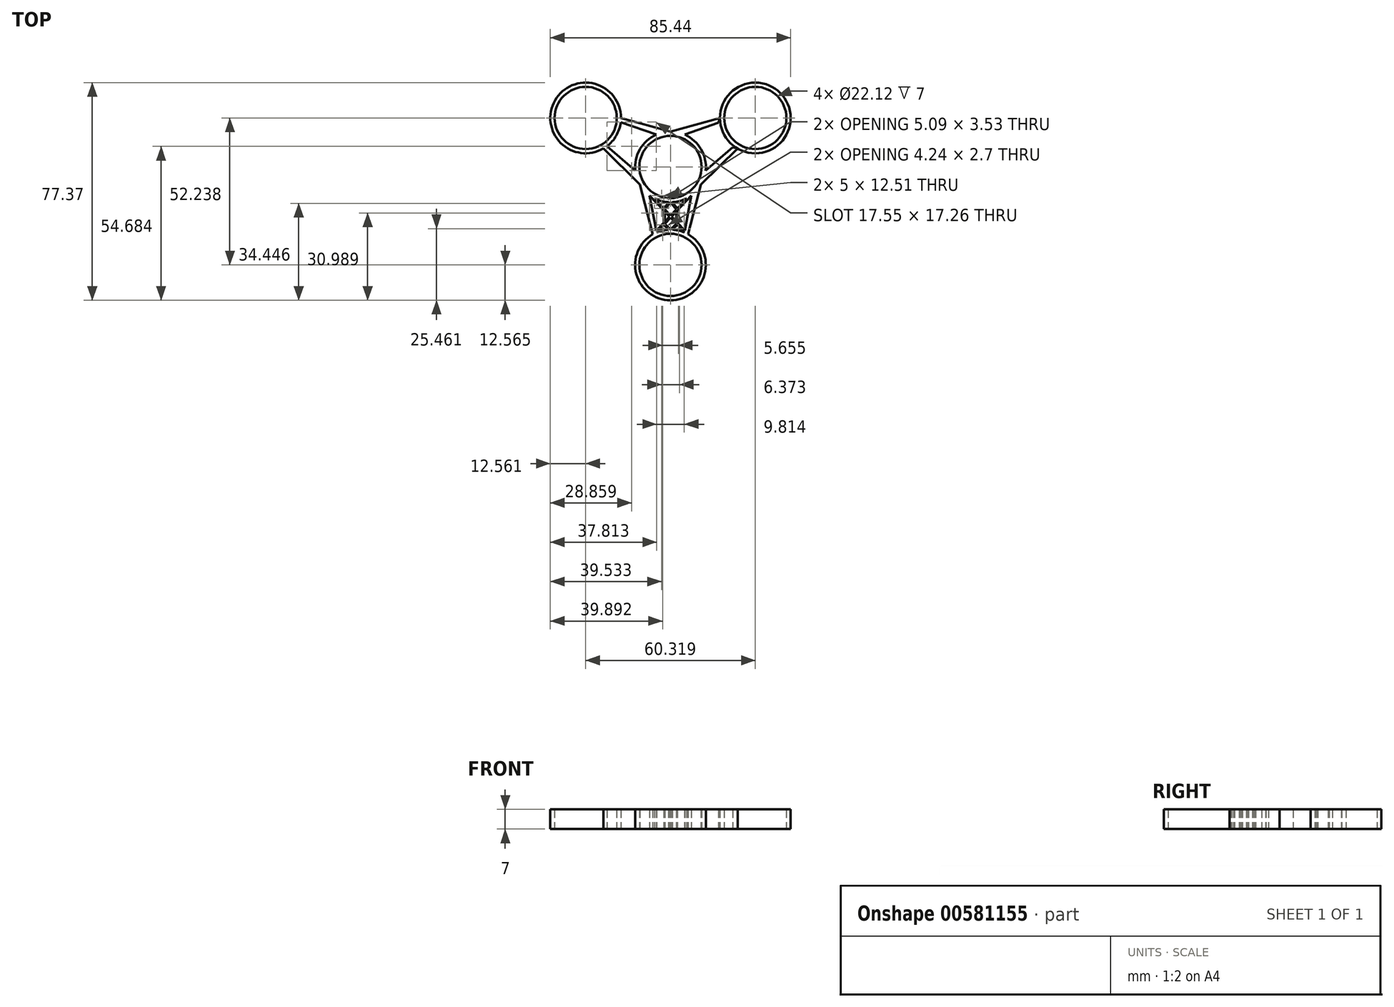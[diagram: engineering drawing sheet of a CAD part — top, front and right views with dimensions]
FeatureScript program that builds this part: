
annotation { "Feature Type Name" : "Feature", "Feature Type Description" : "" }
export const myFeature = defineFeature(function(context is Context, id is Id, definition is map)
    precondition{}
    {
        {
            var Q0;
            Q0=qCreatedBy(makeId("Top.planeOp"),FACE);
            var sketch = newSketch(context, id + "F0", { "sketchPlane" : qUnion([Q0])});
            skCircle(sketch, "E0", {"center": v(0, 0) * mm, "radius": 11.06 * mm});
            skCircle(sketch, "E1", {"center": v(-30.16, 17.41) * mm, "radius": 11.06 * mm});
            skCircle(sketch, "E2", {"center": v(-30.16, 17.41) * mm, "radius": 12.56 * mm});
            skCircle(sketch, "E3", {"center": v(0, -34.82) * mm, "radius": 11.06 * mm});
            skCircle(sketch, "E4", {"center": v(0, -34.82) * mm, "radius": 12.56 * mm});
            skCircle(sketch, "E5", {"center": v(30.16, 17.41) * mm, "radius": 11.06 * mm});
            skCircle(sketch, "E6", {"center": v(30.16, 17.41) * mm, "radius": 12.56 * mm});
            skCircle(sketch, "E7", {"center": v(0, 0) * mm, "radius": 12.56 * mm});
            skLineSegment(sketch, "E8", {"start": v(-30.16, 17.41) * mm, "end": v(0, -34.83) * mm, "construction": true});
            skLineSegment(sketch, "E9", {"start": v(0, -34.82) * mm, "end": v(30.16, 17.41) * mm, "construction": true});
            skLineSegment(sketch, "E10", {"start": v(30.16, 17.41) * mm, "end": v(-30.16, 17.41) * mm, "construction": true});
            skLineSegment(sketch, "E11", {"start": v(0, 0) * mm, "end": v(0, -34.82) * mm, "construction": true});
            skLineSegment(sketch, "E12", {"start": v(-23.88, 6.53) * mm, "end": v(-10.88, -6.28) * mm});
            skLineSegment(sketch, "E13", {"start": v(-10.88, -6.28) * mm, "end": v(-6.28, -23.95) * mm});
            skLineSegment(sketch, "E14", {"start": v(-17.6, 17.41) * mm, "end": v(0, 12.56) * mm});
            skLineSegment(sketch, "E15", {"start": v(0, 12.56) * mm, "end": v(17.6, 17.41) * mm});
            skLineSegment(sketch, "E16", {"start": v(23.88, 6.53) * mm, "end": v(10.88, -6.28) * mm});
            skLineSegment(sketch, "E17", {"start": v(10.88, -6.28) * mm, "end": v(6.28, -23.95) * mm});
            skLineSegment(sketch, "E18", {"start": v(-7.4, -10.15) * mm, "end": v(-4.95, -23.28) * mm});
            skLineSegment(sketch, "E19", {"start": v(7.4, -10.15) * mm, "end": v(4.95, -23.28) * mm});
            skLineSegment(sketch, "E20", {"start": v(12.5, -1.34) * mm, "end": v(22.63, 7.35) * mm});
            skLineSegment(sketch, "E21", {"start": v(17.69, 15.93) * mm, "end": v(5.09, 11.49) * mm});
            skLineSegment(sketch, "E22", {"start": v(-22.63, 7.35) * mm, "end": v(-12.5, -1.34) * mm});
            skLineSegment(sketch, "E23", {"start": v(-5.09, 11.49) * mm, "end": v(-17.69, 15.93) * mm});
            skLineSegment(sketch, "E24", {"start": v(-30.16, 17.41) * mm, "end": v(30.16, 17.41) * mm});
            skLineSegment(sketch, "E25", {"start": v(-4.95, -23.28) * mm, "end": v(7.4, -10.15) * mm});
            skLineSegment(sketch, "E26", {"start": v(4.95, -23.28) * mm, "end": v(-7.4, -10.15) * mm});
            skLineSegment(sketch, "E27", {"start": v(-6.28, -23.95) * mm, "end": v(5.73, -11.18) * mm});
            skLineSegment(sketch, "E28", {"start": v(6.28, -23.95) * mm, "end": v(-5.73, -11.18) * mm});
            skPoint(sketch, "E29", {"position": v(0, -22.26) * mm});
            skPoint(sketch, "E30", {"position": v(0, -18.02) * mm});
            skPoint(sketch, "E31", {"position": v(-0.35, -17.64) * mm});
            skPoint(sketch, "E32", {"position": v(0.35, -17.64) * mm});
            skPoint(sketch, "E33", {"position": v(0, -17.27) * mm});
            skPoint(sketch, "E34", {"position": v(0, -12.56) * mm});
            skLineSegment(sketch, "E35", {"start": v(-2.06, -20.2) * mm, "end": v(0, -22.26) * mm});
            skLineSegment(sketch, "E36", {"start": v(0, -22.26) * mm, "end": v(2.06, -20.2) * mm});
            skLineSegment(sketch, "E37", {"start": v(-2.4, -20.58) * mm, "end": v(-0.7, -22.28) * mm});
            skLineSegment(sketch, "E38", {"start": v(2.4, -20.58) * mm, "end": v(0.7, -22.28) * mm});
            skLineSegment(sketch, "E39", {"start": v(-2.06, -20.2) * mm, "end": v(-2.06, -15.08) * mm});
            skLineSegment(sketch, "E40", {"start": v(-2.4, -20.58) * mm, "end": v(-2.4, -14.7) * mm});
            skLineSegment(sketch, "E41", {"start": v(2.06, -20.2) * mm, "end": v(2.06, -15.08) * mm});
            skLineSegment(sketch, "E42", {"start": v(2.4, -20.58) * mm, "end": v(2.4, -14.7) * mm});
            skLineSegment(sketch, "E43", {"start": v(-2.06, -15.08) * mm, "end": v(0, -12.56) * mm});
            skLineSegment(sketch, "E44", {"start": v(2.06, -15.08) * mm, "end": v(0, -12.56) * mm});
            skLineSegment(sketch, "E45", {"start": v(-2.4, -14.7) * mm, "end": v(-0.64, -12.55) * mm});
            skLineSegment(sketch, "E46", {"start": v(2.4, -14.7) * mm, "end": v(0.64, -12.55) * mm});
            skLineSegment(sketch, "E47", {"start": v(17.69, 15.93) * mm, "end": v(12.5, -1.34) * mm});
            skLineSegment(sketch, "E48", {"start": v(17.6, 17.41) * mm, "end": v(12.55, 0.63) * mm});
            skLineSegment(sketch, "E49", {"start": v(22.63, 7.35) * mm, "end": v(5.09, 11.49) * mm});
            skLineSegment(sketch, "E50", {"start": v(23.88, 6.53) * mm, "end": v(6.82, 10.55) * mm});
            skLineSegment(sketch, "E51", {"start": v(0, 0) * mm, "end": v(30.16, 17.41) * mm, "construction": true});
            skLineSegment(sketch, "E52", {"start": v(0, 0) * mm, "end": v(-30.16, 17.41) * mm, "construction": true});
            skPoint(sketch, "E53", {"position": v(10.88, 6.28) * mm});
            skPoint(sketch, "E54", {"position": v(19.28, 11.13) * mm});
            skPoint(sketch, "E55", {"position": v(15.46, 8.52) * mm});
            skPoint(sketch, "E56", {"position": v(15.1, 9.13) * mm});
            skPoint(sketch, "E57", {"position": v(14.96, 8.63) * mm});
            skPoint(sketch, "E58", {"position": v(15.6, 9) * mm});
            skLineSegment(sketch, "E59", {"start": v(19.28, 11.13) * mm, "end": v(18.53, 8.32) * mm});
            skLineSegment(sketch, "E60", {"start": v(19.28, 11.13) * mm, "end": v(16.47, 11.88) * mm});
            skLineSegment(sketch, "E61", {"start": v(19.65, 10.53) * mm, "end": v(19.03, 8.2) * mm});
            skLineSegment(sketch, "E62", {"start": v(18.94, 11.75) * mm, "end": v(16.62, 12.38) * mm});
            skLineSegment(sketch, "E63", {"start": v(18.53, 8.32) * mm, "end": v(14.22, 6.18) * mm});
            skLineSegment(sketch, "E64", {"start": v(19.03, 8.2) * mm, "end": v(14.06, 5.66) * mm});
            skSolve(sketch);
        }
        {
            var Q0;
            {var subQ0=sQuery(id+"F0.wireOp",EDGE,"E12");Q0=makeQuery(id+"F0.imprint","IMPRINT",FACE,{"disambiguationData":[TD([[makeQuery(id+"F0.imprint","IMPRINT",EDGE,{"derivedFrom":subQ0}),1.0]])]});}
            var Q1;
            Q1=makeQuery(id+"F0.imprint","IMPRINT",FACE,{"disambiguationData":[TD([[makeQuery(id+"F0.imprint","IMPRINT",EDGE,{"derivedFrom":sQuery(id+"F0.wireOp",EDGE,"E1")}),-1.0]])]});
            var Q2;
            {var subQ0=sQuery(id+"F0.wireOp",EDGE,"E14");Q2=makeQuery(id+"F0.imprint","IMPRINT",FACE,{"disambiguationData":[TD([[makeQuery(id+"F0.imprint","IMPRINT",EDGE,{"derivedFrom":subQ0}),-1.0]])]});}
            var Q3;
            Q3=makeQuery(id+"F0.imprint","IMPRINT",FACE,{"disambiguationData":[TD([[makeQuery(id+"F0.imprint","IMPRINT",EDGE,{"derivedFrom":sQuery(id+"F0.wireOp",EDGE,"E0")}),-1.0]])]});
            var Q4;
            {var subQ0=sQuery(id+"F0.wireOp",EDGE,"E15");Q4=makeQuery(id+"F0.imprint","IMPRINT",FACE,{"disambiguationData":[TD([[makeQuery(id+"F0.imprint","IMPRINT",EDGE,{"derivedFrom":subQ0}),-1.0]])]});}
            var Q5;
            {var subQ0=sQuery(id+"F0.wireOp",EDGE,"E16");Q5=makeQuery(id+"F0.imprint","IMPRINT",FACE,{"disambiguationData":[TD([[makeQuery(id+"F0.imprint","IMPRINT",EDGE,{"derivedFrom":subQ0}),-1.0]])]});}
            var Q6;
            Q6=makeQuery(id+"F0.imprint","IMPRINT",FACE,{"disambiguationData":[TD([[makeQuery(id+"F0.imprint","IMPRINT",EDGE,{"derivedFrom":sQuery(id+"F0.wireOp",EDGE,"E5")}),-1.0]])]});
            var Q7;
            Q7=makeQuery(id+"F0.imprint","IMPRINT",FACE,{"disambiguationData":[TD([[makeQuery(id+"F0.imprint","IMPRINT",EDGE,{"derivedFrom":sQuery(id+"F0.wireOp",EDGE,"E3")}),-1.0]])]});
            var Q8;
            {var subQ0=sQuery(id+"F0.wireOp",EDGE,"E17");Q8=makeQuery(id+"F0.imprint","IMPRINT",FACE,{"disambiguationData":[TD([[makeQuery(id+"F0.imprint","IMPRINT",EDGE,{"derivedFrom":subQ0}),-1.0]])]});}
            var Q9;
            {var subQ0=sQuery(id+"F0.wireOp",EDGE,"E13");Q9=makeQuery(id+"F0.imprint","IMPRINT",FACE,{"disambiguationData":[TD([[makeQuery(id+"F0.imprint","IMPRINT",EDGE,{"derivedFrom":subQ0}),1.0]])]});}
            var Q10;
            {var subQ0=sQuery(id+"F0.wireOp",EDGE,"E28");var subQ3=sQuery(id+"F0.wireOp",EDGE,"E19");var subQ5=makeQuery(id+"F0.imprint","INTERSECT",VERTEX,{"derivedFrom":[subQ3,subQ0]});Q10=makeQuery(id+"F0.imprint","IMPRINT",FACE,{"disambiguationData":[TD([[makeQuery(id+"F0.imprint","IMPRINT",EDGE,{"disambiguationData":[TD([[subQ5,-1.0]])],"derivedFrom":subQ3}),1.0]])]});}
            var Q11;
            {var subQ0=sQuery(id+"F0.wireOp",EDGE,"E27");var subQ3=sQuery(id+"F0.wireOp",EDGE,"E18");var subQ5=makeQuery(id+"F0.imprint","INTERSECT",VERTEX,{"derivedFrom":[subQ3,subQ0]});Q11=makeQuery(id+"F0.imprint","IMPRINT",FACE,{"disambiguationData":[TD([[makeQuery(id+"F0.imprint","IMPRINT",EDGE,{"disambiguationData":[TD([[subQ5,-1.0]])],"derivedFrom":subQ3}),-1.0]])]});}
            extrude(context, id + "F1", {"entities" : qUnion([Q0, Q1, Q2, Q3, Q4, Q5, Q6, Q7, Q8, Q9, Q10, Q11]), "depth" : 7 * mm, "offsetDistance" : 25.4 * mm});
        }
        {
            var Q0;
            {var subQ0=sQuery(id+"F0.wireOp",EDGE,"E36");Q0=makeQuery(id+"F0.imprint","IMPRINT",FACE,{"disambiguationData":[TD([[makeQuery(id+"F0.imprint","IMPRINT",EDGE,{"derivedFrom":subQ0}),-1.0]])]});}
            var Q1;
            {var subQ0=sQuery(id+"F0.wireOp",EDGE,"E35");Q1=makeQuery(id+"F0.imprint","IMPRINT",FACE,{"disambiguationData":[TD([[makeQuery(id+"F0.imprint","IMPRINT",EDGE,{"derivedFrom":subQ0}),-1.0]])]});}
            var Q2;
            {var subQ3=sQuery(id+"F0.wireOp",EDGE,"E40");var subQ5=sQuery(id+"F0.wireOp",EDGE,"E27");var subQ6=makeQuery(id+"F0.imprint","INTERSECT",VERTEX,{"derivedFrom":[subQ5,subQ3]});Q2=makeQuery(id+"F0.imprint","IMPRINT",FACE,{"disambiguationData":[TD([[makeQuery(id+"F0.imprint","IMPRINT",EDGE,{"disambiguationData":[TD([[subQ6,-1.0]])],"derivedFrom":subQ5}),-1.0]])]});}
            var Q3;
            {var subQ3=sQuery(id+"F0.wireOp",EDGE,"E42");var subQ5=sQuery(id+"F0.wireOp",EDGE,"E28");var subQ6=makeQuery(id+"F0.imprint","INTERSECT",VERTEX,{"derivedFrom":[subQ5,subQ3]});Q3=makeQuery(id+"F0.imprint","IMPRINT",FACE,{"disambiguationData":[TD([[makeQuery(id+"F0.imprint","IMPRINT",EDGE,{"disambiguationData":[TD([[subQ6,-1.0]])],"derivedFrom":subQ5}),1.0]])]});}
            var Q4;
            {var subQ0=sQuery(id+"F0.wireOp",EDGE,"E41");var subQ1=sQuery(id+"F0.wireOp",EDGE,"E25");var subQ2=makeQuery(id+"F0.imprint","INTERSECT",VERTEX,{"derivedFrom":[subQ1,subQ0]});Q4=makeQuery(id+"F0.imprint","IMPRINT",FACE,{"disambiguationData":[TD([[makeQuery(id+"F0.imprint","IMPRINT",EDGE,{"disambiguationData":[TD([[subQ2,-1.0]])],"derivedFrom":subQ1}),1.0]])]});}
            var Q5;
            {var subQ0=sQuery(id+"F0.wireOp",EDGE,"E39");var subQ1=sQuery(id+"F0.wireOp",EDGE,"E26");var subQ2=makeQuery(id+"F0.imprint","INTERSECT",VERTEX,{"derivedFrom":[subQ1,subQ0]});Q5=makeQuery(id+"F0.imprint","IMPRINT",FACE,{"disambiguationData":[TD([[makeQuery(id+"F0.imprint","IMPRINT",EDGE,{"disambiguationData":[TD([[subQ2,-1.0]])],"derivedFrom":subQ1}),-1.0]])]});}
            var Q6;
            {var subQ0=sQuery(id+"F0.wireOp",EDGE,"E39");var subQ1=sQuery(id+"F0.wireOp",EDGE,"E26");var subQ2=makeQuery(id+"F0.imprint","INTERSECT",VERTEX,{"derivedFrom":[subQ1,subQ0]});Q6=makeQuery(id+"F0.imprint","IMPRINT",FACE,{"disambiguationData":[TD([[makeQuery(id+"F0.imprint","IMPRINT",EDGE,{"disambiguationData":[TD([[subQ2,-1.0]])],"derivedFrom":subQ1}),1.0]])]});}
            var Q7;
            {var subQ0=sQuery(id+"F0.wireOp",EDGE,"E41");var subQ1=sQuery(id+"F0.wireOp",EDGE,"E25");var subQ2=makeQuery(id+"F0.imprint","INTERSECT",VERTEX,{"derivedFrom":[subQ1,subQ0]});Q7=makeQuery(id+"F0.imprint","IMPRINT",FACE,{"disambiguationData":[TD([[makeQuery(id+"F0.imprint","IMPRINT",EDGE,{"disambiguationData":[TD([[subQ2,-1.0]])],"derivedFrom":subQ1}),-1.0]])]});}
            var Q8;
            {var subQ0=sQuery(id+"F0.wireOp",EDGE,"E43");Q8=makeQuery(id+"F0.imprint","IMPRINT",FACE,{"disambiguationData":[TD([[makeQuery(id+"F0.imprint","IMPRINT",EDGE,{"derivedFrom":subQ0}),1.0]])]});}
            var Q9;
            {var subQ0=sQuery(id+"F0.wireOp",EDGE,"E44");Q9=makeQuery(id+"F0.imprint","IMPRINT",FACE,{"disambiguationData":[TD([[makeQuery(id+"F0.imprint","IMPRINT",EDGE,{"derivedFrom":subQ0}),-1.0]])]});}
            var Q10;
            {var subQ1=sQuery(id+"F0.wireOp",EDGE,"E19");var subQ3=sQuery(id+"F0.wireOp",EDGE,"E28");var subQ4=makeQuery(id+"F0.imprint","INTERSECT",VERTEX,{"derivedFrom":[subQ1,subQ3]});Q10=makeQuery(id+"F0.imprint","IMPRINT",FACE,{"disambiguationData":[TD([[makeQuery(id+"F0.imprint","IMPRINT",EDGE,{"disambiguationData":[TD([[subQ4,-1.0]])],"derivedFrom":subQ3}),1.0]])]});}
            var Q11;
            {var subQ1=sQuery(id+"F0.wireOp",EDGE,"E18");var subQ3=sQuery(id+"F0.wireOp",EDGE,"E27");var subQ4=makeQuery(id+"F0.imprint","INTERSECT",VERTEX,{"derivedFrom":[subQ1,subQ3]});Q11=makeQuery(id+"F0.imprint","IMPRINT",FACE,{"disambiguationData":[TD([[makeQuery(id+"F0.imprint","IMPRINT",EDGE,{"disambiguationData":[TD([[subQ4,-1.0]])],"derivedFrom":subQ3}),-1.0]])]});}
            var Q12;
            {var subQ1=sQuery(id+"F0.wireOp",EDGE,"E7");var subQ3=sQuery(id+"F0.wireOp",EDGE,"E27");var subQ4=makeQuery(id+"F0.imprint","INTERSECT",VERTEX,{"derivedFrom":[subQ1,subQ3]});Q12=makeQuery(id+"F0.imprint","IMPRINT",FACE,{"disambiguationData":[TD([[makeQuery(id+"F0.imprint","IMPRINT",EDGE,{"disambiguationData":[TD([[subQ4,-1.0]])],"derivedFrom":subQ1}),-1.0]])]});}
            var Q13;
            {var subQ1=sQuery(id+"F0.wireOp",EDGE,"E7");var subQ3=sQuery(id+"F0.wireOp",EDGE,"E28");var subQ4=makeQuery(id+"F0.imprint","INTERSECT",VERTEX,{"derivedFrom":[subQ1,subQ3]});Q13=makeQuery(id+"F0.imprint","IMPRINT",FACE,{"disambiguationData":[TD([[makeQuery(id+"F0.imprint","IMPRINT",EDGE,{"disambiguationData":[TD([[subQ4,1.0]])],"derivedFrom":subQ1}),-1.0]])]});}
            var Q14;
            {var subQ0=sQuery(id+"F0.wireOp",EDGE,"E26");var subQ1=sQuery(id+"F0.wireOp",EDGE,"E25");var subQ2=makeQuery(id+"F0.imprint","INTERSECT",VERTEX,{"derivedFrom":[subQ1,subQ0]});Q14=makeQuery(id+"F0.imprint","IMPRINT",FACE,{"disambiguationData":[TD([[makeQuery(id+"F0.imprint","IMPRINT",EDGE,{"disambiguationData":[TD([[subQ2,-1.0]])],"derivedFrom":subQ1}),-1.0]])]});}
            var Q15;
            {var subQ0=sQuery(id+"F0.wireOp",EDGE,"E26");var subQ1=sQuery(id+"F0.wireOp",EDGE,"E25");var subQ2=makeQuery(id+"F0.imprint","INTERSECT",VERTEX,{"derivedFrom":[subQ1,subQ0]});Q15=makeQuery(id+"F0.imprint","IMPRINT",FACE,{"disambiguationData":[TD([[makeQuery(id+"F0.imprint","IMPRINT",EDGE,{"disambiguationData":[TD([[subQ2,-1.0]])],"derivedFrom":subQ1}),1.0]])]});}
            var Q16;
            {var subQ0=sQuery(id+"F0.wireOp",EDGE,"E28");var subQ1=sQuery(id+"F0.wireOp",EDGE,"E25");var subQ2=makeQuery(id+"F0.imprint","INTERSECT",VERTEX,{"derivedFrom":[subQ1,subQ0]});Q16=makeQuery(id+"F0.imprint","IMPRINT",FACE,{"disambiguationData":[TD([[makeQuery(id+"F0.imprint","IMPRINT",EDGE,{"disambiguationData":[TD([[subQ2,-1.0]])],"derivedFrom":subQ1}),1.0]])]});}
            extrude(context, id + "F2", {"entities" : qUnion([Q0, Q1, Q2, Q3, Q4, Q5, Q6, Q7, Q8, Q9, Q10, Q11, Q12, Q13, Q14, Q15, Q16]), "operationType" : NewBodyOperationType.ADD, "depth" : 7 * mm, "offsetDistance" : 25.4 * mm});
        }
        {
            var Q0;
            {var subQ1=sQuery(id+"F0.wireOp",EDGE,"E25");var subQ3=sQuery(id+"F0.wireOp",EDGE,"E26");var subQ4=makeQuery(id+"F0.imprint","INTERSECT",VERTEX,{"derivedFrom":[subQ1,subQ3]});Q0=makeQuery(id+"F0.imprint","IMPRINT",FACE,{"disambiguationData":[TD([[makeQuery(id+"F0.imprint","IMPRINT",EDGE,{"disambiguationData":[TD([[subQ4,-1.0]])],"derivedFrom":subQ3}),1.0]])]});}
            var Q1;
            {var subQ0=sQuery(id+"F0.wireOp",EDGE,"E27");var subQ1=sQuery(id+"F0.wireOp",EDGE,"E26");var subQ2=makeQuery(id+"F0.imprint","INTERSECT",VERTEX,{"derivedFrom":[subQ1,subQ0]});Q1=makeQuery(id+"F0.imprint","IMPRINT",FACE,{"disambiguationData":[TD([[makeQuery(id+"F0.imprint","IMPRINT",EDGE,{"disambiguationData":[TD([[subQ2,-1.0]])],"derivedFrom":subQ1}),-1.0]])]});}
            extrude(context, id + "F3", {"entities" : qUnion([Q0, Q1]), "operationType" : NewBodyOperationType.ADD, "depth" : 7 * mm, "offsetDistance" : 25.4 * mm});
        }
    });
